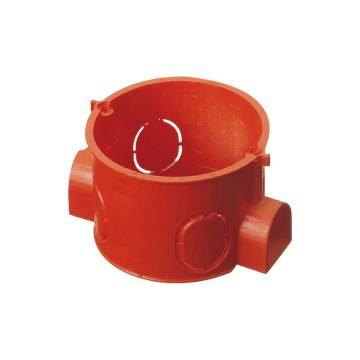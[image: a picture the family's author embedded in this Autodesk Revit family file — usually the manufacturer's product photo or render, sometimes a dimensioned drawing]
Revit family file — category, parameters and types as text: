
# Revit family: Building-ContenitoriIncasso-GEWISS-24SC-SCATOLE-INCASSO_TONDA_COMPONIBILE
name_source: partatom
category: Apparecchi elettrici
revit_build: Autodesk Revit 2016 (Build: 20161004_0715(x64)
units: mm (PartAtom-declared; Revit-internal decimal feet)

## family parameters
Condiviso = Sì
Host = Muro
Mantenere orientamento annotazione = Sì
Numero OmniClass = 23.80.30.14.24
Punto di calcolo locali = Sì
Quota connettore circolare = Usa diametro
Sempre verticale = Sì
Taglio con vuoti quando caricato = Sì
Tipo di parte = Normale
Titolo OmniClass = Junction Boxes

## types (1)
- GW24232 - Scatola rotonda componibile
    Caratteristiche = Halogen free
    Catalogo = BUILDING
    Catalogo Serie = 24SC
    Codice EAN = 8011564072312
    Codice Electrocod = 0210
    Descrizione = SCATOLA ROTONDA COMPONIBILE
    Descrizione: = Tonda componibile
    Dimensioni (mm) = Ã˜60x42
    Glow Wire Test = 650°C
    IDF = 9676771c-21f7-43f8-bcd4-0edc71109c78
    IDT = d3faba48-2ce0-441e-8284-55e0996afa80
    Immagine tipo = GW24232.jpg
    Installazione = Incasso
    Interasse fissaggio supporti = 60MM
    Modello = GW24232
    Per Pareti = Muratura
    Produttore = GEWISS S.p.A.
    SEO = Scatola
    Scheda Tecnica = https://www.gewiss.com
    Temperatura di impiego = -15 +60 °C
    Termopressione con biglia = 70 °C
    URL = https://www.gewiss.com
    Versione file RFA = 19.0
